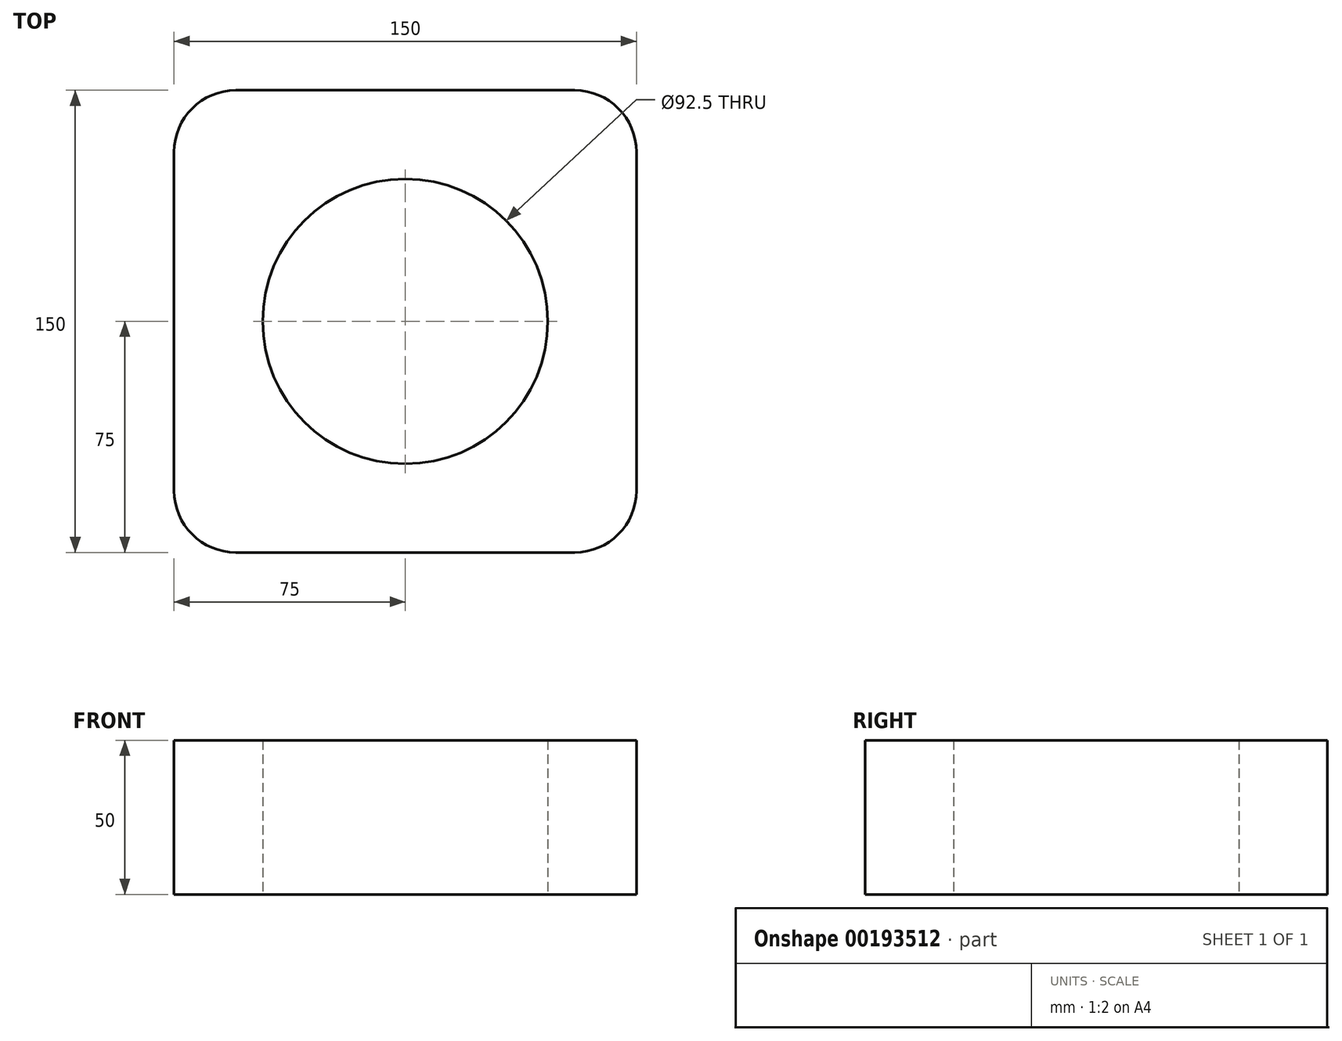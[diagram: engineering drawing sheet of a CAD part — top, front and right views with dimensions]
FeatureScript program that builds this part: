
annotation { "Feature Type Name" : "Feature", "Feature Type Description" : "" }
export const myFeature = defineFeature(function(context is Context, id is Id, definition is map)
    precondition{}
    {
        {
            var Q0;
            Q0=qCreatedBy(makeId("Top.planeOp"),FACE);
            var sketch = newSketch(context, id + "F0", { "sketchPlane" : qUnion([Q0])});
            skLineSegment(sketch, "E0.bottom", {"start": v(-75, 75) * mm, "end": v(75, 75) * mm});
            skLineSegment(sketch, "E0.top", {"start": v(-75, -75) * mm, "end": v(75, -75) * mm});
            skLineSegment(sketch, "E0.left", {"start": v(-75, 75) * mm, "end": v(-75, -75) * mm});
            skLineSegment(sketch, "E0.right", {"start": v(75, 75) * mm, "end": v(75, -75) * mm});
            skPoint(sketch, "E0.middle", {"position": v(0, 0) * mm});
            skSolve(sketch);
        }
        {
            var Q0;
            Q0=makeQuery(id+"F0.imprint","IMPRINT",FACE,{"disambiguationData":[TD([[makeQuery(id+"F0.imprint","IMPRINT",EDGE,{"derivedFrom":sQuery(id+"F0.wireOp",EDGE,"E0.bottom")}),-1.0]])]});
            extrude(context, id + "F1", {"entities" : qUnion([Q0]), "depth" : 50 * mm});
        }
        {
            var Q0;
            Q0=makeQuery(id+"F1.opExtrude","CAP_FACE",FACE,{"disambiguationData":[OSD([sQuery(id+"F0.wireOp",EDGE,"E0.bottom"),sQuery(id+"F0.wireOp",EDGE,"E0.top"),sQuery(id+"F0.wireOp",EDGE,"E0.left"),sQuery(id+"F0.wireOp",EDGE,"E0.right")])],"isStart":true});
            var sketch = newSketch(context, id + "F2", { "sketchPlane" : qUnion([Q0])});
            skCircle(sketch, "E1", {"center": v(0, 0) * mm, "radius": 46.25 * mm});
            skSolve(sketch);
        }
        {
            var Q0;
            Q0=makeQuery(id+"F2.imprint","IMPRINT",FACE,{"disambiguationData":[TD([[makeQuery(id+"F2.imprint","IMPRINT",EDGE,{"derivedFrom":sQuery(id+"F2.wireOp",EDGE,"E1")}),1.0]])]});
            var Q1;
            Q1=sQuery(id+"F2.wireOp",EDGE,"E1");
            extrude(context, id + "F3", {"entities" : qUnion([Q0]), "operationType" : NewBodyOperationType.REMOVE, "surfaceEntities" : qUnion([Q1]), "oppositeDirection" : true, "depth" : 50 * mm});
        }
        {
            var Q0;
            Q0=makeQuery(id+"F1.opExtrude","SWEPT_EDGE",EDGE,{"disambiguationData":[OSD([sQuery(id+"F0.wireOp",EDGE,"E0.top"),sQuery(id+"F0.wireOp",EDGE,"E0.right")])]});
            var Q1;
            Q1=makeQuery(id+"F1.opExtrude","SWEPT_EDGE",EDGE,{"disambiguationData":[OSD([sQuery(id+"F0.wireOp",EDGE,"E0.bottom"),sQuery(id+"F0.wireOp",EDGE,"E0.right")])]});
            fillet(context, id + "F4", {"entities" : qUnion([Q0, Q1]), "radius" : 20 * mm, "tangentPropagation" : true, "allowEdgeOverflow" : false});
        }
        {
            var Q0;
            Q0=makeQuery(id+"F1.opExtrude","SWEPT_EDGE",EDGE,{"disambiguationData":[OSD([sQuery(id+"F0.wireOp",EDGE,"E0.top"),sQuery(id+"F0.wireOp",EDGE,"E0.left")])]});
            fillet(context, id + "F5", {"entities" : qUnion([Q0]), "radius" : 20 * mm, "tangentPropagation" : true, "allowEdgeOverflow" : false});
        }
        {
            var Q0;
            Q0=makeQuery(id+"F1.opExtrude","SWEPT_EDGE",EDGE,{"disambiguationData":[OSD([sQuery(id+"F0.wireOp",EDGE,"E0.bottom"),sQuery(id+"F0.wireOp",EDGE,"E0.left")])]});
            fillet(context, id + "F6", {"entities" : qUnion([Q0]), "radius" : 20 * mm, "tangentPropagation" : true, "allowEdgeOverflow" : false});
        }
    });
